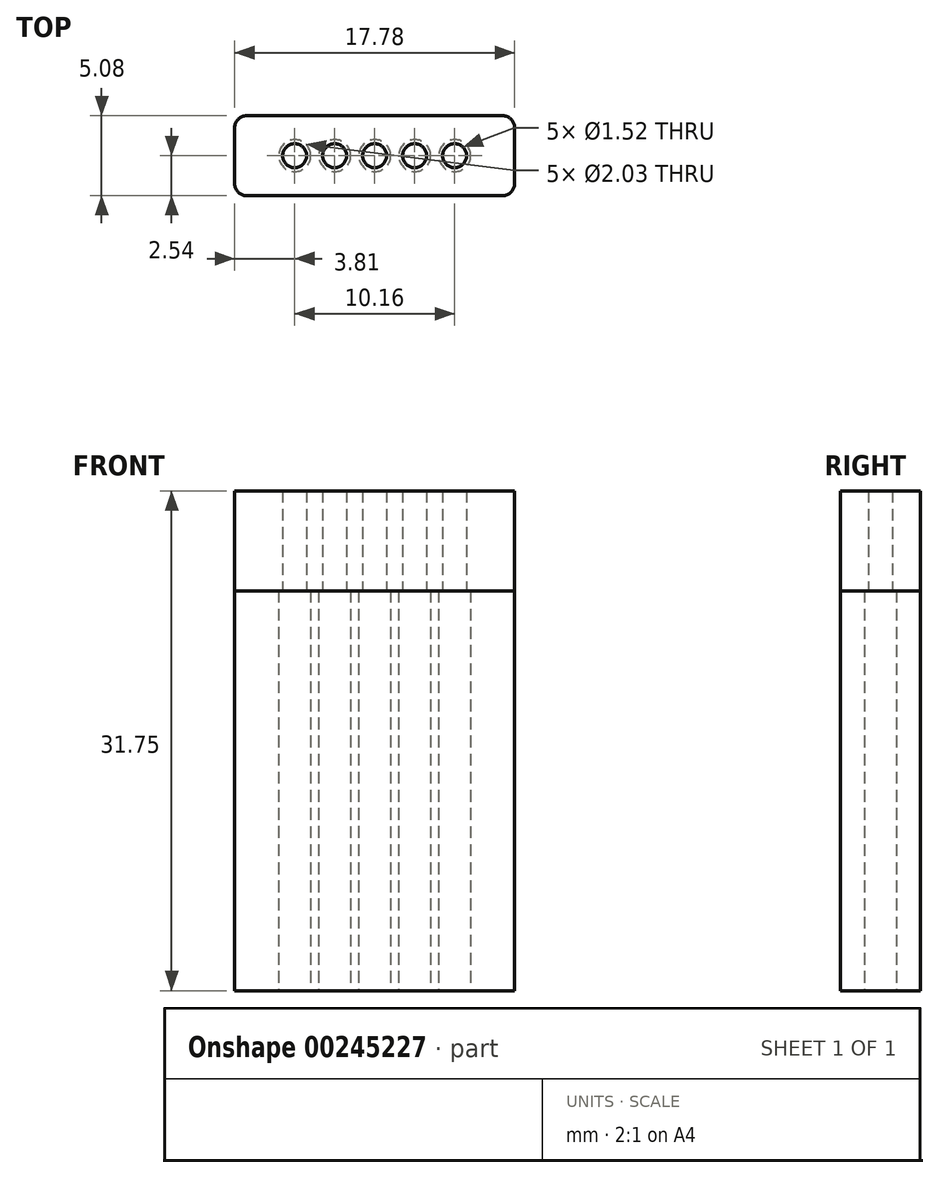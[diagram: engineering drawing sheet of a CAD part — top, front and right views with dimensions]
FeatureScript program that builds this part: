
annotation { "Feature Type Name" : "Feature", "Feature Type Description" : "" }
export const myFeature = defineFeature(function(context is Context, id is Id, definition is map)
    precondition{}
    {
        {
            var Q0;
            Q0=qCreatedBy(makeId("Top.planeOp"),FACE);
            var sketch = newSketch(context, id + "F0", { "sketchPlane" : qUnion([Q0])});
            skLineSegment(sketch, "E0.bottom", {"start": v(8.13, -2.54) * mm, "end": v(-8.13, -2.54) * mm});
            skLineSegment(sketch, "E0.top", {"start": v(8.13, 2.54) * mm, "end": v(-8.13, 2.54) * mm});
            skLineSegment(sketch, "E0.left", {"start": v(8.9, -1.78) * mm, "end": v(8.9, 1.78) * mm});
            skLineSegment(sketch, "E0.right", {"start": v(-8.9, -1.78) * mm, "end": v(-8.9, 1.78) * mm});
            skPoint(sketch, "E0.middle", {"position": v(0, 0) * mm});
            skCircle(sketch, "E1", {"center": v(0, 0) * mm, "radius": 1.02 * mm});
            skCircle(sketch, "E2.1.0.0", {"center": v(2.54, 0) * mm, "radius": 1.02 * mm});
            skCircle(sketch, "E2.2.0.0", {"center": v(5.08, 0) * mm, "radius": 1.02 * mm});
            skLineSegment(sketch, "E2.direction1", {"start": v(0, 0) * mm, "end": v(2.54, 0) * mm, "construction": true});
            skCircle(sketch, "E3.1.0.0", {"center": v(-2.54, 0) * mm, "radius": 1.02 * mm});
            skCircle(sketch, "E3.2.0.0", {"center": v(-5.08, 0) * mm, "radius": 1.02 * mm});
            skLineSegment(sketch, "E3.direction1", {"start": v(0, 0) * mm, "end": v(-2.54, 0) * mm, "construction": true});
            skPoint(sketch, "E4.visualSharp", {"position": v(-8.9, 2.54) * mm});
            skArc(sketch, "E4.filletArc", {"start": v(-8.13, 2.54) * mm, "mid": v(-8.67, 2.32) * mm, "end": v(-8.9, 1.78) * mm});
            skPoint(sketch, "E5.visualSharp", {"position": v(8.9, 2.54) * mm});
            skArc(sketch, "E5.filletArc", {"start": v(8.9, 1.78) * mm, "mid": v(8.67, 2.32) * mm, "end": v(8.13, 2.54) * mm});
            skPoint(sketch, "E6.visualSharp", {"position": v(8.9, -2.54) * mm});
            skArc(sketch, "E6.filletArc", {"start": v(8.13, -2.54) * mm, "mid": v(8.67, -2.32) * mm, "end": v(8.9, -1.78) * mm});
            skPoint(sketch, "E7.visualSharp", {"position": v(-8.9, -2.54) * mm});
            skArc(sketch, "E7.filletArc", {"start": v(-8.9, -1.78) * mm, "mid": v(-8.67, -2.32) * mm, "end": v(-8.13, -2.54) * mm});
            skSolve(sketch);
        }
        {
            var Q0;
            Q0=makeQuery(id+"F0.imprint","IMPRINT",FACE,{"disambiguationData":[TD([[makeQuery(id+"F0.imprint","IMPRINT",EDGE,{"derivedFrom":sQuery(id+"F0.wireOp",EDGE,"E0.bottom")}),-1.0]])]});
            extrude(context, id + "F1", {"entities" : qUnion([Q0]), "depth" : 25.4 * mm});
        }
        {
            var Q0;
            Q0=makeQuery(id+"F1.opExtrude","CAP_FACE",FACE,{"disambiguationData":[OSD([sQuery(id+"F0.wireOp",EDGE,"E0.bottom"),sQuery(id+"F0.wireOp",EDGE,"E0.top"),sQuery(id+"F0.wireOp",EDGE,"E0.left"),sQuery(id+"F0.wireOp",EDGE,"E0.right"),sQuery(id+"F0.wireOp",EDGE,"E1"),sQuery(id+"F0.wireOp",EDGE,"E2.1.0.0"),sQuery(id+"F0.wireOp",EDGE,"E2.2.0.0"),sQuery(id+"F0.wireOp",EDGE,"E3.1.0.0"),sQuery(id+"F0.wireOp",EDGE,"E3.2.0.0"),sQuery(id+"F0.wireOp",EDGE,"E4.filletArc"),sQuery(id+"F0.wireOp",EDGE,"E5.filletArc"),sQuery(id+"F0.wireOp",EDGE,"E6.filletArc"),sQuery(id+"F0.wireOp",EDGE,"E7.filletArc")])],"isStart":false});
            var sketch = newSketch(context, id + "F2", { "sketchPlane" : qUnion([Q0])});
            skLineSegment(sketch, "E8.0", {"start": v(8.13, 2.54) * mm, "end": v(-8.13, 2.54) * mm});
            skArc(sketch, "E9.0", {"start": v(-8.13, 2.54) * mm, "mid": v(-8.67, 2.32) * mm, "end": v(-8.9, 1.78) * mm});
            skLineSegment(sketch, "E10.0", {"start": v(-8.9, -1.78) * mm, "end": v(-8.9, 1.78) * mm});
            skArc(sketch, "E11.0", {"start": v(-8.9, -1.78) * mm, "mid": v(-8.67, -2.32) * mm, "end": v(-8.13, -2.54) * mm});
            skLineSegment(sketch, "E12.0", {"start": v(8.13, -2.54) * mm, "end": v(-8.13, -2.54) * mm});
            skArc(sketch, "E13.0", {"start": v(8.13, -2.54) * mm, "mid": v(8.67, -2.32) * mm, "end": v(8.9, -1.78) * mm});
            skLineSegment(sketch, "E14.0", {"start": v(8.9, -1.78) * mm, "end": v(8.9, 1.78) * mm});
            skPoint(sketch, "E15.0", {"position": v(8.67, 2.32) * mm});
            skArc(sketch, "E16.0", {"start": v(8.9, 1.78) * mm, "mid": v(8.67, 2.32) * mm, "end": v(8.13, 2.54) * mm});
            skPoint(sketch, "E17", {"position": v(-5.08, 0) * mm});
            skPoint(sketch, "E18", {"position": v(-2.54, 0) * mm});
            skPoint(sketch, "E19", {"position": v(0, 0) * mm});
            skPoint(sketch, "E20", {"position": v(2.54, 0) * mm});
            skPoint(sketch, "E21", {"position": v(5.08, 0) * mm});
            skCircle(sketch, "E22", {"center": v(-5.08, 0) * mm, "radius": 0.76 * mm});
            skCircle(sketch, "E23.1.0.0", {"center": v(-2.54, 0) * mm, "radius": 0.76 * mm});
            skCircle(sketch, "E23.2.0.0", {"center": v(0, 0) * mm, "radius": 0.76 * mm});
            skCircle(sketch, "E23.3.0.0", {"center": v(2.54, 0) * mm, "radius": 0.76 * mm});
            skCircle(sketch, "E23.4.0.0", {"center": v(5.08, 0) * mm, "radius": 0.76 * mm});
            skLineSegment(sketch, "E23.direction1", {"start": v(-5.08, 0) * mm, "end": v(-2.54, 0) * mm, "construction": true});
            skSolve(sketch);
        }
        {
            var Q0;
            Q0 = qSketchRegion(id + "F2", true);
            extrude(context, id + "F3", {"entities" : qUnion([Q0]), "depth" : 6.35 * mm});
        }
    });
